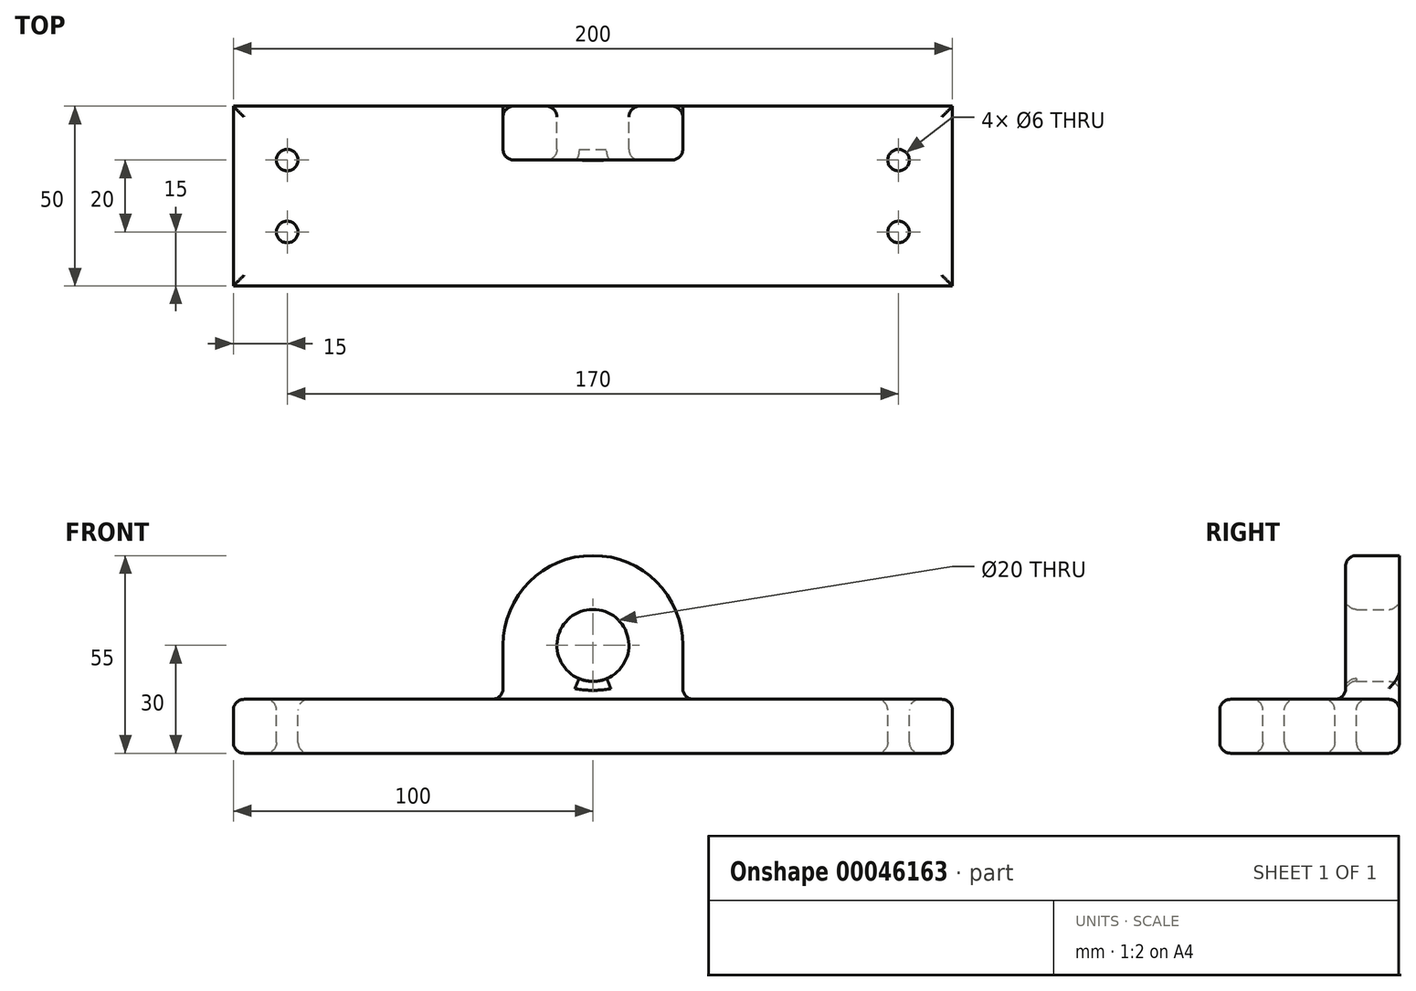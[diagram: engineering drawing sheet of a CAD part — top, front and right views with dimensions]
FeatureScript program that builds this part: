
annotation { "Feature Type Name" : "Feature", "Feature Type Description" : "" }
export const myFeature = defineFeature(function(context is Context, id is Id, definition is map)
    precondition{}
    {
        {
            var Q0;
            Q0=qCreatedBy(makeId("Top.planeOp"),FACE);
            var sketch = newSketch(context, id + "F0", { "sketchPlane" : qUnion([Q0])});
            skLineSegment(sketch, "E0.rect.bottom", {"start": v(100, 25) * mm, "end": v(-100, 25) * mm});
            skLineSegment(sketch, "E0.rect.top", {"start": v(100, -25) * mm, "end": v(-100, -25) * mm});
            skLineSegment(sketch, "E0.rect.left", {"start": v(100, 25) * mm, "end": v(100, -25) * mm});
            skLineSegment(sketch, "E0.rect.right", {"start": v(-100, 25) * mm, "end": v(-100, -25) * mm});
            skPoint(sketch, "E0.rect.middle", {"position": v(0, 0) * mm});
            skSolve(sketch);
        }
        {
            var Q0;
            Q0=qSketchRegion(id+"F0",true);
            extrude(context, id + "F1", {"entities" : qUnion([Q0]), "depth" : 15 * mm});
        }
        {
            var Q0;
            Q0=makeQuery(id+"F1.opExtrude","SWEPT_FACE",FACE,{"disambiguationData":[OSD([sQuery(id+"F0.wireOp",EDGE,"E0.rect.bottom")])]});
            var sketch = newSketch(context, id + "F2", { "sketchPlane" : qUnion([Q0])});
            skLineSegment(sketch, "E1", {"start": v(0, 0) * mm, "end": v(0, 30) * mm, "construction": true});
            skCircle(sketch, "E2", {"center": v(0, 30) * mm, "radius": 25 * mm});
            skLineSegment(sketch, "E3.bottom", {"start": v(-25, 30) * mm, "end": v(25, 30) * mm});
            skLineSegment(sketch, "E3.top", {"start": v(-25, 0) * mm, "end": v(25, 0) * mm});
            skLineSegment(sketch, "E3.left", {"start": v(-25, 30) * mm, "end": v(-25, 0) * mm});
            skLineSegment(sketch, "E3.right", {"start": v(25, 30) * mm, "end": v(25, 0) * mm});
            skCircle(sketch, "E4", {"center": v(0, 30) * mm, "radius": 10 * mm});
            skSolve(sketch);
        }
        {
            var Q0;
            {var subQ0=sQuery(id+"F2.wireOp",EDGE,"E4");var subQ1=sQuery(id+"F2.wireOp",EDGE,"E3.bottom");var subQ3=makeQuery(id+"F2.imprint","INTERSECT",VERTEX,{"disambiguationData":[OD(0.0)],"derivedFrom":[subQ1,subQ0]});Q0=makeQuery(id+"F2.imprint","IMPRINT",FACE,{"disambiguationData":[TD([[makeQuery(id+"F2.imprint","IMPRINT",EDGE,{"disambiguationData":[TD([[subQ3,1.0]])],"derivedFrom":subQ0}),-1.0]])]});}
            var Q1;
            {var subQ0=makeQuery(id+"F1.opExtrude","CAP_EDGE",EDGE,{"disambiguationData":[OSD([sQuery(id+"F0.wireOp",EDGE,"E0.rect.bottom")])],"isStart":false});var subQ3=sQuery(id+"F2.wireOp",EDGE,"E3.right");var subQ4=makeQuery(id+"F2.imprint","INTERSECT",VERTEX,{"derivedFrom":[subQ0,subQ3]});Q1=makeQuery(id+"F2.imprint","IMPRINT",FACE,{"disambiguationData":[TD([[makeQuery(id+"F2.imprint","IMPRINT",EDGE,{"disambiguationData":[TD([[subQ4,1.0]])],"derivedFrom":subQ0}),1.0]])]});}
            var Q2;
            {var subQ3=sQuery(id+"F2.wireOp",EDGE,"E3.bottom");var subQ7=sQuery(id+"F2.wireOp",EDGE,"E4");var subQ8=makeQuery(id+"F2.imprint","INTERSECT",VERTEX,{"disambiguationData":[OD(0.0)],"derivedFrom":[subQ3,subQ7]});Q2=makeQuery(id+"F2.imprint","IMPRINT",FACE,{"disambiguationData":[TD([[makeQuery(id+"F2.imprint","IMPRINT",EDGE,{"disambiguationData":[TD([[subQ8,-1.0]])],"derivedFrom":subQ7}),-1.0]])]});}
            var Q3;
            {var subQ0=makeQuery(id+"F1.opExtrude","CAP_EDGE",EDGE,{"disambiguationData":[OSD([sQuery(id+"F0.wireOp",EDGE,"E0.rect.bottom")])],"isStart":false});var subQ3=sQuery(id+"F2.wireOp",EDGE,"E3.left");var subQ4=makeQuery(id+"F2.imprint","INTERSECT",VERTEX,{"derivedFrom":[subQ0,subQ3]});Q3=makeQuery(id+"F2.imprint","IMPRINT",FACE,{"disambiguationData":[TD([[makeQuery(id+"F2.imprint","IMPRINT",EDGE,{"disambiguationData":[TD([[subQ4,-1.0]])],"derivedFrom":subQ0}),1.0]])]});}
            extrude(context, id + "F3", {"entities" : qUnion([Q0, Q1, Q2, Q3]), "operationType" : NewBodyOperationType.ADD, "oppositeDirection" : true, "depth" : 15 * mm});
        }
        {
            var Q0;
            Q0=makeQuery(id+"F1.opExtrude","CAP_FACE",FACE,{"disambiguationData":[OSD([sQuery(id+"F0.wireOp",EDGE,"E0.rect.bottom"),sQuery(id+"F0.wireOp",EDGE,"E0.rect.top"),sQuery(id+"F0.wireOp",EDGE,"E0.rect.left"),sQuery(id+"F0.wireOp",EDGE,"E0.rect.right")])],"isStart":false});
            var sketch = newSketch(context, id + "F4", { "sketchPlane" : qUnion([Q0])});
            skLineSegment(sketch, "E5.rect.bottom", {"start": v(-85, 10) * mm, "end": v(85, 10) * mm, "construction": true});
            skLineSegment(sketch, "E5.rect.top", {"start": v(-85, -10) * mm, "end": v(85, -10) * mm, "construction": true});
            skLineSegment(sketch, "E5.rect.left", {"start": v(-85, 10) * mm, "end": v(-85, -10) * mm, "construction": true});
            skLineSegment(sketch, "E5.rect.right", {"start": v(85, 10) * mm, "end": v(85, -10) * mm, "construction": true});
            skPoint(sketch, "E5.rect.middle", {"position": v(0, 0) * mm});
            skCircle(sketch, "E6", {"center": v(-85, 10) * mm, "radius": 3 * mm});
            skCircle(sketch, "E7", {"center": v(-85, -10) * mm, "radius": 3 * mm});
            skCircle(sketch, "E8", {"center": v(85, -10) * mm, "radius": 3 * mm});
            skCircle(sketch, "E9", {"center": v(85, 10) * mm, "radius": 3 * mm});
            skSolve(sketch);
        }
        {
            var Q0;
            Q0=makeQuery(id+"F4.imprint","IMPRINT",FACE,{"disambiguationData":[TD([[makeQuery(id+"F4.imprint","IMPRINT",EDGE,{"derivedFrom":sQuery(id+"F4.wireOp",EDGE,"E6")}),1.0]])]});
            var Q1;
            Q1=makeQuery(id+"F4.imprint","IMPRINT",FACE,{"disambiguationData":[TD([[makeQuery(id+"F4.imprint","IMPRINT",EDGE,{"derivedFrom":sQuery(id+"F4.wireOp",EDGE,"E7")}),1.0]])]});
            var Q2;
            Q2=makeQuery(id+"F4.imprint","IMPRINT",FACE,{"disambiguationData":[TD([[makeQuery(id+"F4.imprint","IMPRINT",EDGE,{"derivedFrom":sQuery(id+"F4.wireOp",EDGE,"E8")}),1.0]])]});
            var Q3;
            Q3=makeQuery(id+"F4.imprint","IMPRINT",FACE,{"disambiguationData":[TD([[makeQuery(id+"F4.imprint","IMPRINT",EDGE,{"derivedFrom":sQuery(id+"F4.wireOp",EDGE,"E9")}),1.0]])]});
            extrude(context, id + "F5", {"entities" : qUnion([Q0, Q1, Q2, Q3]), "operationType" : NewBodyOperationType.REMOVE, "oppositeDirection" : true, "depth" : 25 * mm});
        }
        {
            var Q0;
            Q0=makeQuery(id+"F1.opExtrude","CAP_FACE",FACE,{"disambiguationData":[OSD([sQuery(id+"F0.wireOp",EDGE,"E0.rect.bottom"),sQuery(id+"F0.wireOp",EDGE,"E0.rect.top"),sQuery(id+"F0.wireOp",EDGE,"E0.rect.left"),sQuery(id+"F0.wireOp",EDGE,"E0.rect.right")])],"isStart":false});
            var Q1;
            Q1=makeQuery(id+"F1.opExtrude","CAP_FACE",FACE,{"disambiguationData":[OSD([sQuery(id+"F0.wireOp",EDGE,"E0.rect.bottom"),sQuery(id+"F0.wireOp",EDGE,"E0.rect.top"),sQuery(id+"F0.wireOp",EDGE,"E0.rect.left"),sQuery(id+"F0.wireOp",EDGE,"E0.rect.right")])],"isStart":true});
            var Q2;
            Q2=makeQuery(id+"F3.opExtrude","CAP_EDGE",EDGE,{"disambiguationData":[OSD([sQuery(id+"F2.wireOp",EDGE,"E4")])],"isStart":true});
            var Q3;
            Q3=makeQuery(id+"F3.opExtrude","CAP_EDGE",EDGE,{"disambiguationData":[OSD([sQuery(id+"F2.wireOp",EDGE,"E2")])],"isStart":false});
            fillet(context, id + "F6", {"entities" : qUnion([Q0, Q1, Q2, Q3]), "radius" : 3 * mm, "tangentPropagation" : true, "allowEdgeOverflow" : false});
        }
        {
            var Q0;
            Q0=makeQuery(id+"F3.opExtrude","CAP_EDGE",EDGE,{"disambiguationData":[OSD([sQuery(id+"F2.wireOp",EDGE,"E4")])],"isStart":false});
            fillet(context, id + "F7", {"entities" : qUnion([Q0]), "radius" : 3 * mm, "tangentPropagation" : true, "allowEdgeOverflow" : false});
        }
    });
